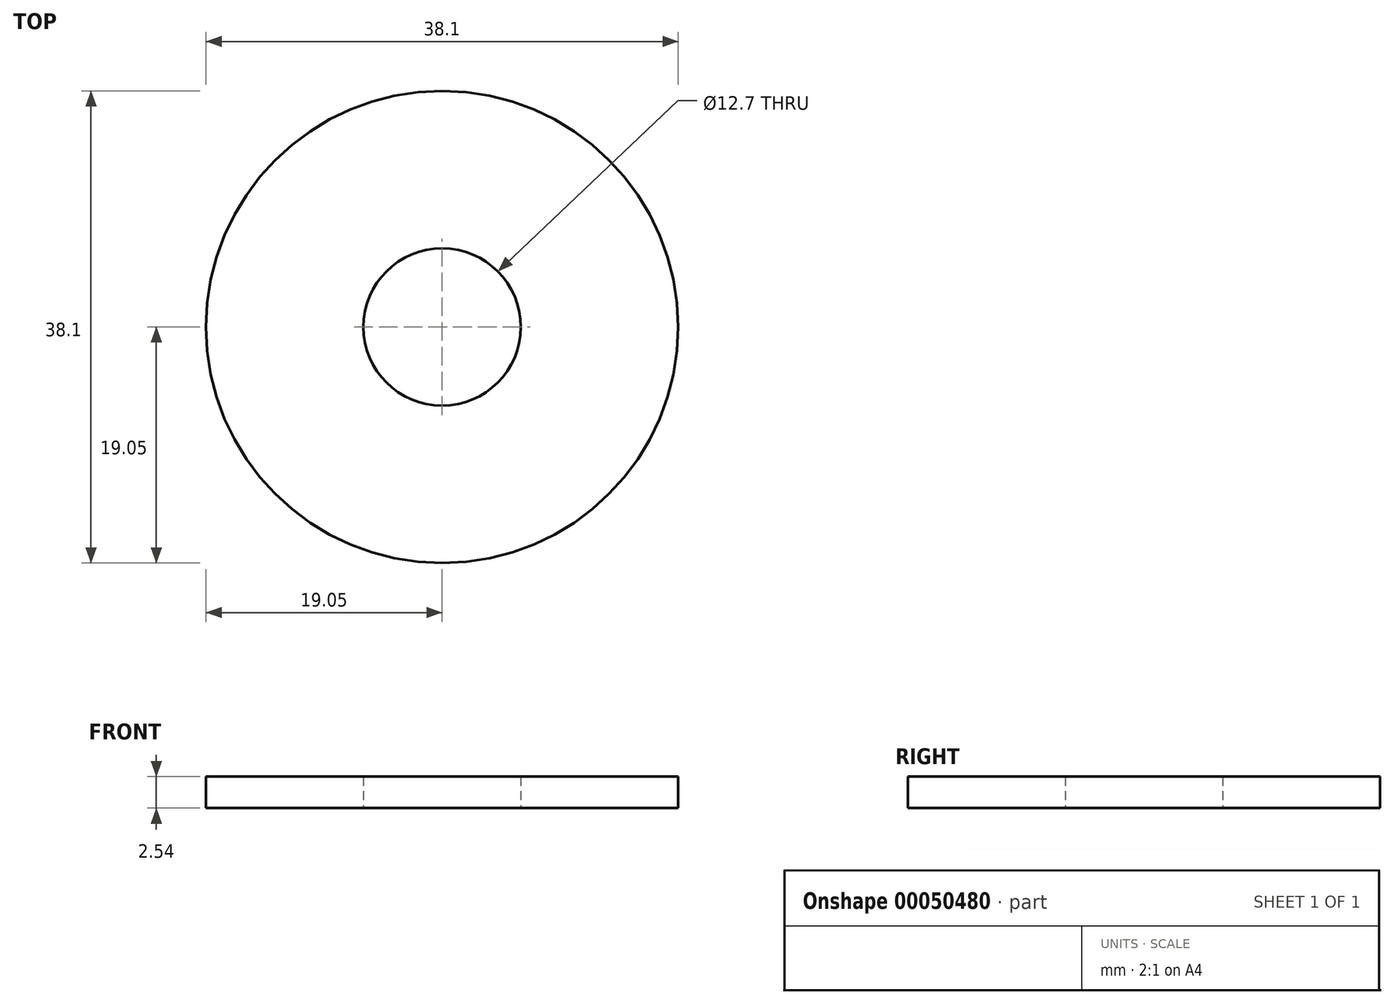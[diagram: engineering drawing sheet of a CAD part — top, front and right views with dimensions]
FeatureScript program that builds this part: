
annotation { "Feature Type Name" : "Feature", "Feature Type Description" : "" }
export const myFeature = defineFeature(function(context is Context, id is Id, definition is map)
    precondition{}
    {
        {
            var Q0;
            Q0=qCreatedBy(makeId("Top.planeOp"),FACE);
            var sketch = newSketch(context, id + "F0", { "sketchPlane" : qUnion([Q0])});
            skCircle(sketch, "E0", {"center": v(0, 0) * mm, "radius": 19.05 * mm});
            skCircle(sketch, "E1", {"center": v(0, 0) * mm, "radius": 6.35 * mm});
            skSolve(sketch);
        }
        {
            var Q0;
            Q0=qSketchRegion(id+"F0",true);
            extrude(context, id + "F1", {"entities" : qUnion([Q0]), "endBound" : BoundingType.SYMMETRIC, "depth" : 2.54 * mm});
        }
    });
